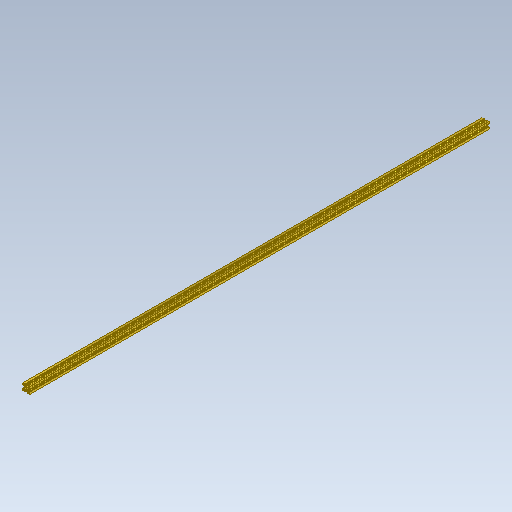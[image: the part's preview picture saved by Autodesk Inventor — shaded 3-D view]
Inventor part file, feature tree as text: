
AUTODESK INVENTOR PART (.ipt)
format: ipt  version: 2025.2 (Build 292293000, 293)  size: 349,696 bytes
history: native  units: mm
features: mirror x4, extrude x1, sketch x1
ambient origin geometry x8: Origin, YZ Plane, XZ Plane, XY Plane, X Axis, Y Axis, Z Axis, Center Point
bodies: Body1 (feature_tree)
feature tree (6):
  extrude  "Extrusão7"  Depth=0.5mm
  mirror  "Espelhar15"
  mirror  "Espelhar16"
  mirror  "Espelhar17"
  mirror  "Espelhar18"
  sketch  "Esboço1"  dims[d0=10.0mm d1=15.0mm d2=30.0mm d5=8.2mm d7=1.1mm d10=4.5mm d13=1.1mm d14=11.5mm d21=2.2mm d39=2000.0mm d40=0.0mm d41=0.5mm d42=2.0mm d44=8.0mm d29=0.5mm d30=0.872665mm d31=0.5mm d32=0.872665mm d33=0.5mm d34=0.872665mm d35=0.5mm d36=0.872665mm d37=0.5mm d38=0.872665mm]
